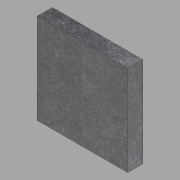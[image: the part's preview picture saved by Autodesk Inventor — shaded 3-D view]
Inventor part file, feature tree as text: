
AUTODESK INVENTOR PART (.ipt)
format: ipt  version: 2022.1 (Build 261234020, 234B)  size: 97,280 bytes
history: native  units: in
note: dims shown in document units (in); Inventor stores cm internally (conversion verified against a paired STEP export)
features: extrude x1, sketch x1
ambient origin geometry x8: Origin, YZ Plane, XZ Plane, XY Plane, X Axis, Y Axis, Z Axis, Center Point
bodies: Solid1 (feature_tree)
feature tree (2):
  extrude  "Extrusion1"  Depth=36.0in
  sketch  "Sketch1"  dims[d0=36.0in d1=36.0in d2=6.0in d3=0.0in]
